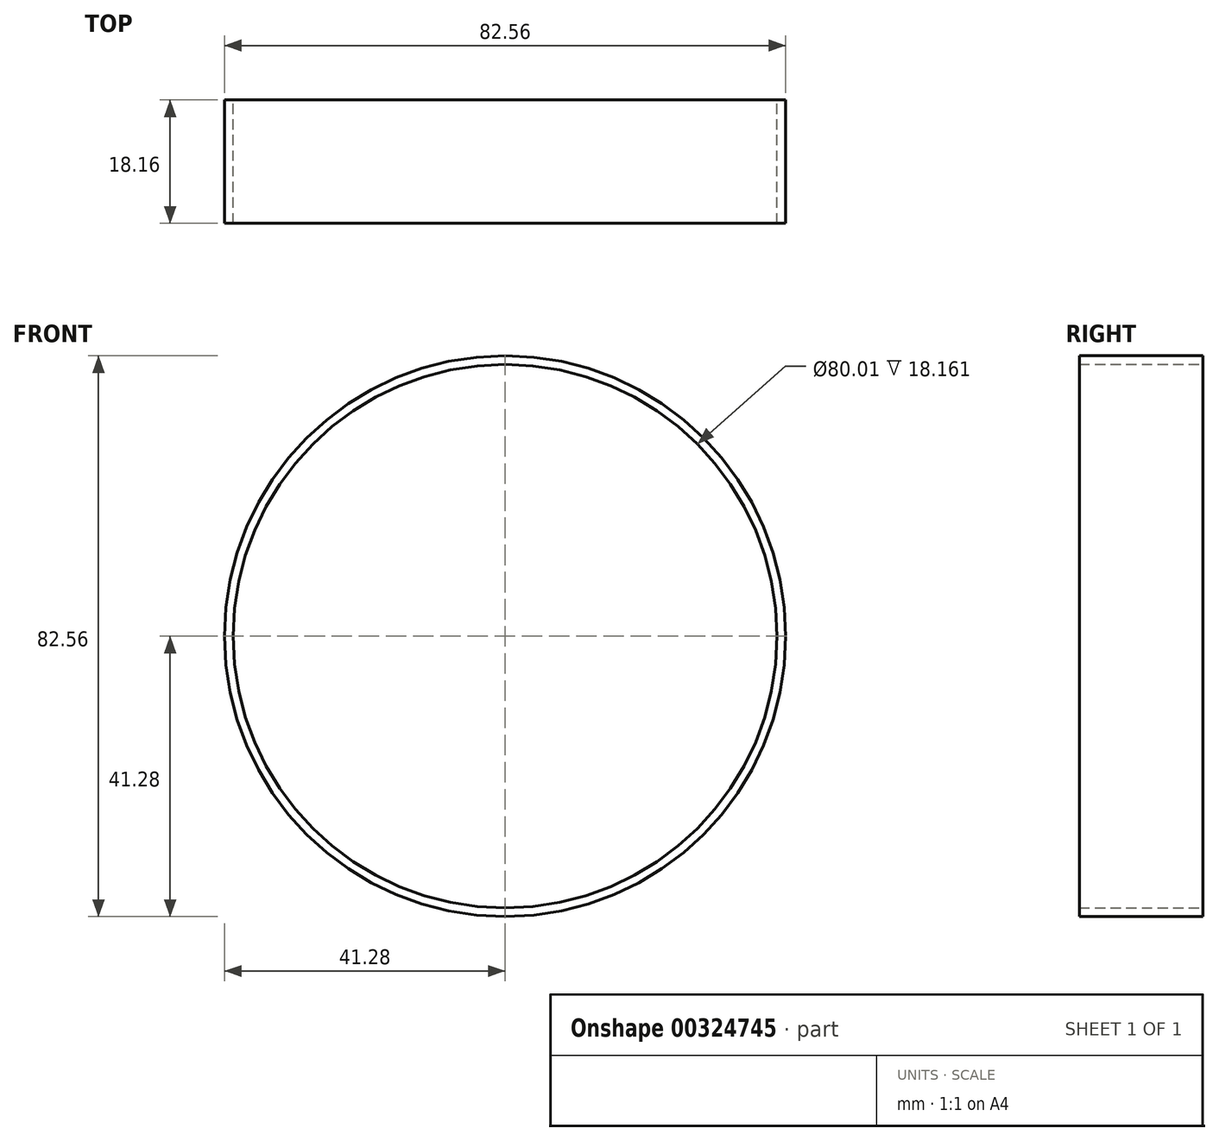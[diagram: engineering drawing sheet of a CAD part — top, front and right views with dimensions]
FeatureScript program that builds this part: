
annotation { "Feature Type Name" : "Feature", "Feature Type Description" : "" }
export const myFeature = defineFeature(function(context is Context, id is Id, definition is map)
    precondition{}
    {
        {
            var Q0;
            Q0=qCreatedBy(makeId("Front.planeOp"),FACE);
            var sketch = newSketch(context, id + "F0", { "sketchPlane" : qUnion([Q0])});
            skCircle(sketch, "E0", {"center": v(0, 0) * mm, "radius": 41.28 * mm});
            skCircle(sketch, "E1", {"center": v(0, 0) * mm, "radius": 40 * mm});
            skSolve(sketch);
        }
        {
            var Q0;
            Q0=makeQuery(id+"F0.imprint","IMPRINT",FACE,{"disambiguationData":[TD([[makeQuery(id+"F0.imprint","IMPRINT",EDGE,{"derivedFrom":sQuery(id+"F0.wireOp",EDGE,"E0")}),1.0]])]});
            extrude(context, id + "F1", {"entities" : qUnion([Q0]), "depth" : 18.16 * mm, "offsetDistance" : 25.4 * mm});
        }
    });
